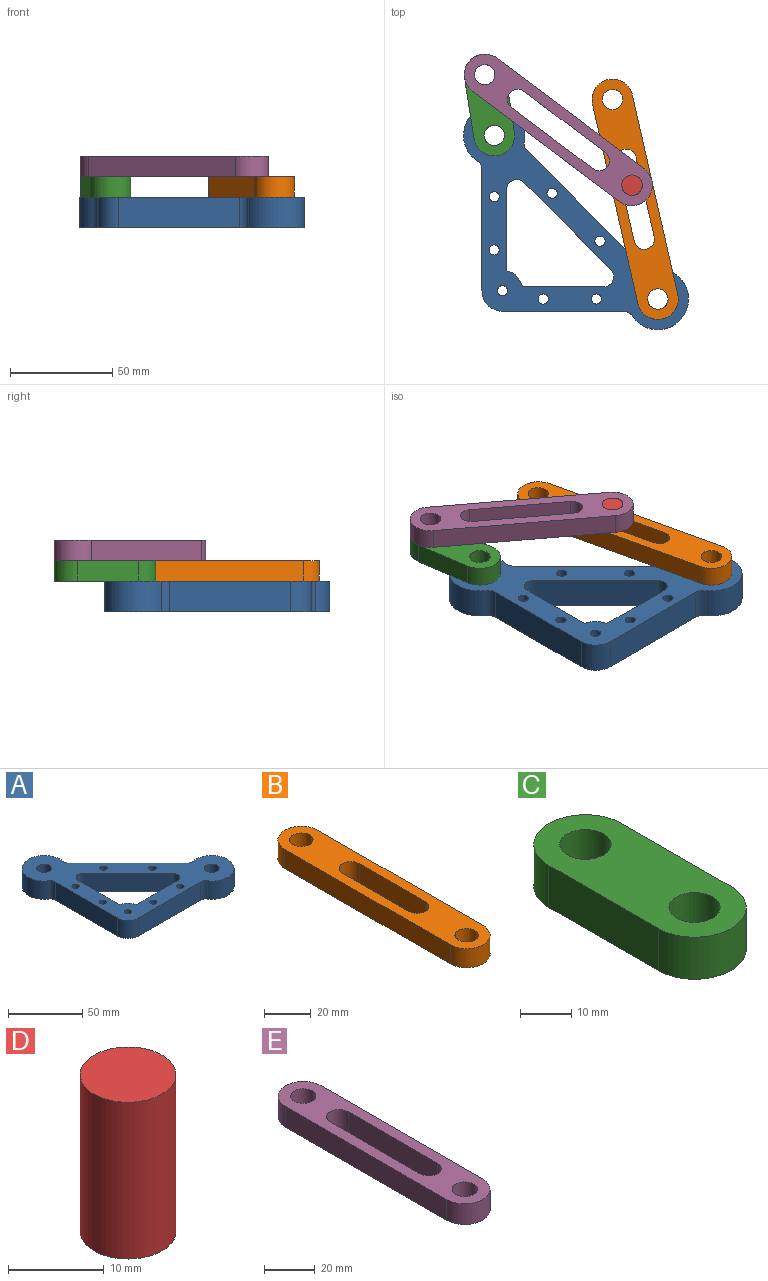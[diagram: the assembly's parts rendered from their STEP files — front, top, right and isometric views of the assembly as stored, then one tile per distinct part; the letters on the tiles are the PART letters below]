
ASSEMBLY  parts=5 mates=5
PART A: 27 faces, bbox 110x110x15 mm
  f0: cylinder r=10mm len=15mm, axis (0,0,-1), area 235.6mm2, adj f1,f15,f16,f17
  f1: plane 59.3x15mm, normal (0,-1,0), area 889.5mm2, adj f0,f2,f16,f17
  f2: cylinder r=5mm len=15mm, axis (0,0,-1), area 74.1mm2, adj f1,f3,f16,f17
  f3: cylinder r=15mm len=30mm, axis (0,0,-1), area 974.9mm2, adj f2,f4,f16,f17
  f4: cylinder r=5mm len=15mm, axis (0,0,-1), area 74.1mm2, adj f3,f5,f16,f17
  f5: plane 56.38x56.38mm, normal (0.71,0.71,0), area 1196mm2, adj f4,f6,f16,f17
  f6: cylinder r=5mm len=15mm, axis (0,0,-1), area 74.1mm2, adj f5,f7,f16,f17
  f7: cylinder r=15mm len=30mm, axis (0,0,-1), area 974.9mm2, adj f6,f8,f16,f17
  f8: cylinder r=5mm len=15mm, axis (0,0,-1), area 74.1mm2, adj f7,f15,f16,f17
  f9: plane 39.65x15mm, normal (1,0,0), area 594.7mm2, adj f10,f14,f16,f17
  f10: cylinder r=5mm len=15mm, axis (0,0,-1), area 176.7mm2, adj f9,f11,f16,f17
  f11: plane 42.44x42.44mm, normal (-0.71,-0.71,0), area 900.4mm2, adj f10,f12,f16,f17
  f12: cylinder r=5mm len=15mm, axis (0,0,-1), area 176.7mm2, adj f11,f13,f16,f17
  f13: plane 39.65x15mm, normal (0,1,0), area 594.7mm2, adj f12,f14,f16,f17
  f14: cylinder r=10mm len=15mm, axis (0,0,-1), area 175.2mm2, adj f9,f13,f16,f17
  f15: plane 59.3x15mm, normal (-1,0,0), area 889.5mm2, adj f0,f8,f16,f17
  f16: plane 110x110mm, normal (0,0,1), area 3784.6mm2, adj f0,f1,f2,f3,f4,f5,f6,f7
  f17: plane 110x110mm, normal (0,0,-1), area 3784.6mm2, adj f0,f1,f2,f3,f4,f5,f6,f7
  f18: cylinder r=5mm len=15mm, axis (0,0,1), area 471.2mm2, adj f16,f17
  f19: cylinder r=5mm len=15mm, axis (0,0,1), area 471.2mm2, adj f16,f17
  f20: cylinder r=2.5mm len=15mm, axis (0,0,1), area 235.6mm2, adj f16,f17
  f21: cylinder r=2.5mm len=15mm, axis (0,0,1), area 235.6mm2, adj f16,f17
  f22: cylinder r=2.5mm len=15mm, axis (0,0,1), area 235.6mm2, adj f16,f17
  f23: cylinder r=2.5mm len=15mm, axis (0,0,1), area 235.6mm2, adj f16,f17
  f24: cylinder r=2.5mm len=15mm, axis (0,0,1), area 235.6mm2, adj f16,f17
  f25: cylinder r=2.5mm len=15mm, axis (0,0,1), area 235.6mm2, adj f16,f17
  f26: cylinder r=2.5mm len=15mm, axis (0,0,1), area 235.6mm2, adj f16,f17
PART B: 12 faces, bbox 20x120x10 mm
  f0: plane 100x10mm, normal (1,0,0), area 1000mm2, adj f1,f7,f8,f9
  f1: cylinder r=10mm len=20mm, axis (0,0,-1), area 314.2mm2, adj f0,f2,f8,f9
  f2: plane 100x10mm, normal (-1,0,0), area 1000mm2, adj f1,f7,f8,f9
  f3: cylinder r=5mm len=10mm, axis (0,0,-1), area 157.1mm2, adj f4,f6,f8,f9
  f4: plane 40x10mm, normal (-1,0,0), area 400mm2, adj f3,f5,f8,f9
  f5: cylinder r=5mm len=10mm, axis (0,0,-1), area 157.1mm2, adj f4,f6,f8,f9
  f6: plane 40x10mm, normal (1,0,0), area 400mm2, adj f3,f5,f8,f9
  f7: cylinder r=10mm len=20mm, axis (0,0,-1), area 314.2mm2, adj f0,f2,f8,f9
  f8: plane 120x20mm, normal (0,0,1), area 1678.5mm2, adj f0,f1,f2,f3,f4,f5,f6,f7
  f9: plane 120x20mm, normal (0,0,-1), area 1678.5mm2, adj f0,f1,f2,f3,f4,f5,f6,f7
  f10: cylinder r=5mm len=10mm, axis (0,0,1), area 314.2mm2, adj f8,f9
  f11: cylinder r=5mm len=10mm, axis (0,0,1), area 314.2mm2, adj f8,f9
PART C: 8 faces, bbox 20x50x10 mm
  f0: plane 30x10mm, normal (1,0,0), area 300mm2, adj f1,f3,f4,f5
  f1: cylinder r=10mm len=20mm, axis (0,0,-1), area 314.2mm2, adj f0,f2,f4,f5
  f2: plane 30x10mm, normal (-1,0,0), area 300mm2, adj f1,f3,f4,f5
  f3: cylinder r=10mm len=20mm, axis (0,0,-1), area 314.2mm2, adj f0,f2,f4,f5
  f4: plane 50x20mm, normal (0,0,1), area 757.1mm2, adj f0,f1,f2,f3,f6,f7
  f5: plane 50x20mm, normal (0,0,-1), area 757.1mm2, adj f0,f1,f2,f3,f6,f7
  f6: cylinder r=5mm len=10mm, axis (0,0,1), area 314.2mm2, adj f4,f5
  f7: cylinder r=5mm len=10mm, axis (0,0,1), area 314.2mm2, adj f4,f5
PART D: 3 faces, bbox 10x10x20 mm
  f0: cylinder r=5mm len=20mm, axis (0,0,-1), area 628.3mm2, adj f1,f2
  f1: plane 10x10mm, normal (0,0,1), area 78.5mm2, adj f0
  f2: plane 10x10mm, normal (0,0,-1), area 78.5mm2, adj f0
PART E: 12 faces, bbox 20x110x10 mm
  f0: plane 90x10mm, normal (1,0,0), area 900mm2, adj f1,f7,f8,f9
  f1: cylinder r=10mm len=20mm, axis (0,0,-1), area 314.2mm2, adj f0,f2,f8,f9
  f2: plane 90x10mm, normal (-1,0,0), area 900mm2, adj f1,f7,f8,f9
  f3: cylinder r=5mm len=10mm, axis (0,0,-1), area 157.1mm2, adj f4,f6,f8,f9
  f4: plane 50x10mm, normal (-1,0,0), area 500mm2, adj f3,f5,f8,f9
  f5: cylinder r=5mm len=10mm, axis (0,0,-1), area 157.1mm2, adj f4,f6,f8,f9
  f6: plane 50x10mm, normal (1,0,0), area 500mm2, adj f3,f5,f8,f9
  f7: cylinder r=10mm len=20mm, axis (0,0,-1), area 314.2mm2, adj f0,f2,f8,f9
  f8: plane 110x20mm, normal (0,0,1), area 1378.5mm2, adj f0,f1,f2,f3,f4,f5,f6,f7
  f9: plane 110x20mm, normal (0,0,-1), area 1378.5mm2, adj f0,f1,f2,f3,f4,f5,f6,f7
  f10: cylinder r=5mm len=10mm, axis (0,0,1), area 314.2mm2, adj f8,f9
  f11: cylinder r=5mm len=10mm, axis (0,0,1), area 314.2mm2, adj f8,f9
PLACE A t=(40.39,-40.08,-7.95)mm fixed
PLACE B rot(axis=(0,0,1),12.8deg) t=(18.23,57.44,7.05)mm
PLACE C rot(axis=(0,0,1),8.8deg) t=(-44.22,69.57,7.05)mm
PLACE D rot(axis=(0,0,-1),36.9deg) t=(27.75,15.53,7.05)mm
PLACE E rot(axis=(0,0,1),53.1deg) t=(-44.22,69.57,17.05)mm
MATE fastened D.f0 <-> E.f7  axis (0,0,1) through (27.75,15.53,27.05)mm
MATE revolute A.f7 <-> C.f3  axis (0,0,1) through (-39.61,39.92,7.05)mm
MATE revolute B.f7 <-> A.f3  axis (0,0,-1) through (40.39,-40.08,7.05)mm
MATE revolute E.f10 <-> C.f6  axis (0,0,1) through (-44.22,69.57,17.05)mm
MATE pin_slot D.f0 <-> B.f3  axis (0,0,-1) through (27.75,15.53,7.05)mm
